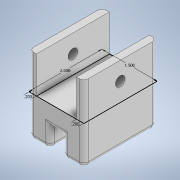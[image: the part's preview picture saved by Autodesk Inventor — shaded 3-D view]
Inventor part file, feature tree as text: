
AUTODESK INVENTOR PART (.ipt)
format: ipt  version: 2020 (Build 240168000, 168)  size: 194,560 bytes
history: native  units: in
note: dims shown in document units (in); Inventor stores cm internally (conversion verified against a paired STEP export)
features: sketch x3, extrude x3, fillet x2, hole x1
ambient origin geometry x8: Origin, YZ Plane, XZ Plane, XY Plane, X Axis, Y Axis, Z Axis, Center Point
bodies: Solid1 (feature_tree)
feature tree (9):
  sketch  "Sketch1"  dims[d0=1.5in d1=2.0in]
  extrude  "Extrusion1"  Depth=2.0in
  extrude  "Extrusion2"  Depth=0.2in
  hole  "Hole1"  [1 undecoded]
  extrude  "Extrusion3"  Depth=0.125in
  fillet  "Fillet1"  Radius=0.75in
  fillet  "Fillet2"  Radius=0.35in
  sketch  "Sketch2"  dims[d2=0.2in d3=0.2in]
  sketch  "Sketch3"  dims[d4=1.0in d5=0.0in d6=0.55in d7=0.0in d8=0.5in d9=0.266in d10=0.75in d11=0.438in d12=0.25in d13=0.5635in d14=1.0in d15=0.8108in d16=0.75in d17=0.35in d18=0.78in d19=0.55in d20=0.0in d21=0.125in d22=0.125in]
note: 1 required parameter value undecoded (feature->parameter linkage not recoverable at this tier; creation-order binding heuristic only, values carry confidence <= 0.55)
